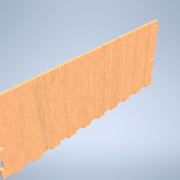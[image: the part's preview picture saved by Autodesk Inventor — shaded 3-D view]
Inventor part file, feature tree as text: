
AUTODESK INVENTOR PART (.ipt)
format: ipt  version: 2021 (Build 250183000, 183)  size: 253,952 bytes
history: native  units: mm
features: extrude x4, sketch x4
ambient origin geometry x8: Origin, YZ Plane, XZ Plane, XY Plane, X Axis, Y Axis, Z Axis, Center Point
bodies: Solid1 (feature_tree)
feature tree (8):
  extrude  "Extrusion1"  Depth=200.0mm
  extrude  "Extrusion2"  Depth=10.0mm
  extrude  "Extrusion3"  Depth=10.0mm
  extrude  "Extrusion4"  Depth=10.0mm
  sketch  "Sketch1"  dims[d0=77.0mm d1=200.0mm]
  sketch  "Sketch2"  dims[d2=3.0mm d3=0.0mm d4=10.0mm]
  sketch  "Sketch3"  dims[d7=100.0mm d9=20.0mm d10=10.0mm d12=10.0mm d14=10.0mm]
  sketch  "Sketch4"  dims[d15=3.0mm d16=10.0mm d17=30.0mm d19=20.0mm d20=10.0mm d22=10.0mm d24=10.0mm d25=10.0mm d26=3.0mm d27=0.0mm d28=10.0mm d29=3.0mm d30=10.0mm d31=20.0mm d32=3.0mm d33=0.0mm d34=4.0mm d35=3.0mm d36=20.0mm d38=190.0mm d39=20.0mm d41=41.0mm d44=0.0mm d45=0.0mm]
